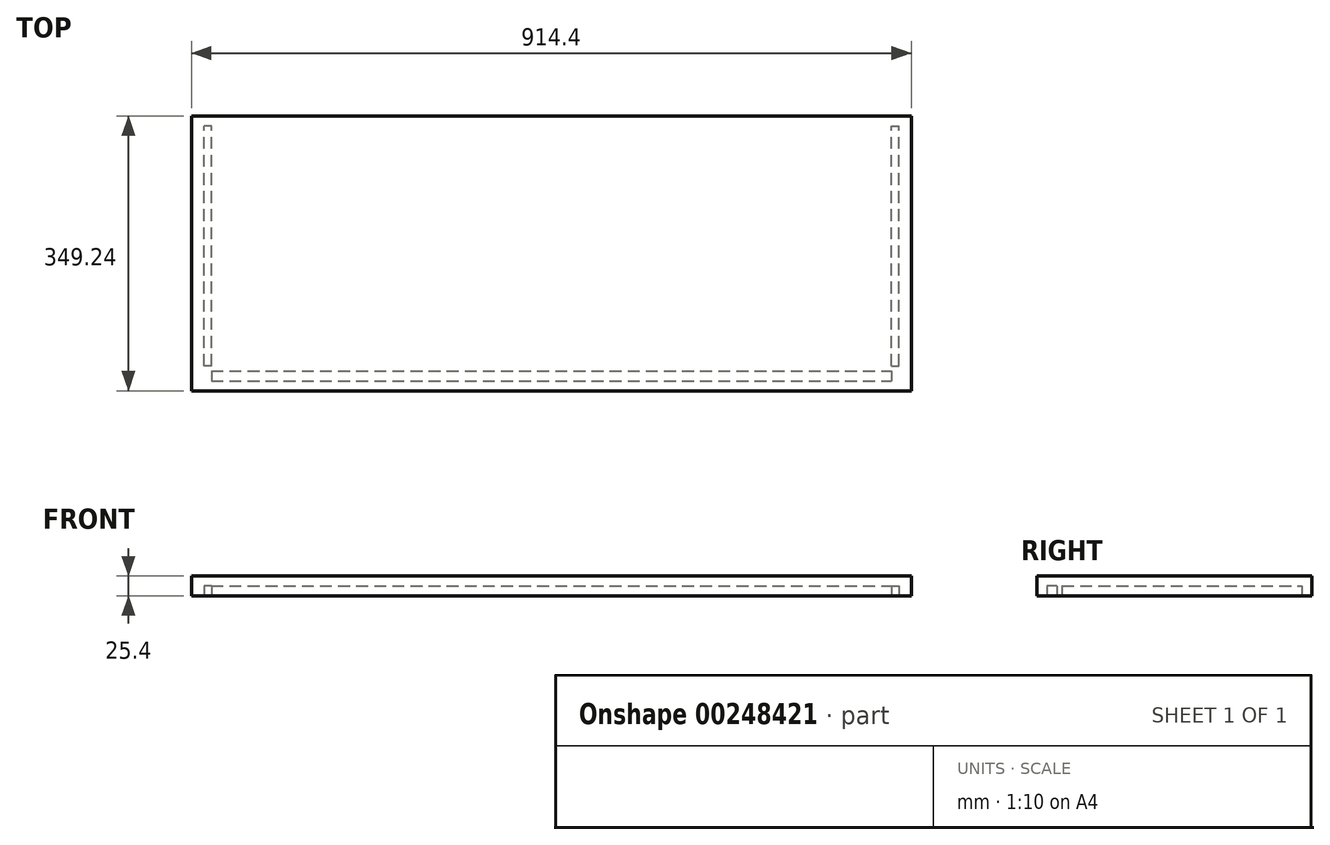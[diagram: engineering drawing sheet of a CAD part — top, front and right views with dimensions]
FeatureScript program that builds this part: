
annotation { "Feature Type Name" : "Feature", "Feature Type Description" : "" }
export const myFeature = defineFeature(function(context is Context, id is Id, definition is map)
    precondition{}
    {
        {
            var Q0;
            Q0=qCreatedBy(makeId("Top.planeOp"),FACE);
            var sketch = newSketch(context, id + "F0", { "sketchPlane" : qUnion([Q0])});
            skLineSegment(sketch, "E0.bottom", {"start": v(-457.2, 174.62) * mm, "end": v(457.2, 174.62) * mm});
            skLineSegment(sketch, "E0.top", {"start": v(-457.2, -174.62) * mm, "end": v(457.2, -174.62) * mm});
            skLineSegment(sketch, "E0.left", {"start": v(-457.2, 174.62) * mm, "end": v(-457.2, -174.62) * mm});
            skLineSegment(sketch, "E0.right", {"start": v(457.2, 174.62) * mm, "end": v(457.2, -174.62) * mm});
            skPoint(sketch, "E0.middle", {"position": v(0, 0) * mm});
            skSolve(sketch);
        }
        {
            var Q0;
            Q0=makeQuery(id+"F0.imprint","IMPRINT",FACE,{"disambiguationData":[TD([[makeQuery(id+"F0.imprint","IMPRINT",EDGE,{"derivedFrom":sQuery(id+"F0.wireOp",EDGE,"E0.bottom")}),-1.0]])]});
            var Q1;
            Q1=makeQuery(id+"F0.imprint","IMPRINT",FACE,{"disambiguationData":[TD([[makeQuery(id+"F0.imprint","IMPRINT",EDGE,{"derivedFrom":sQuery(id+"F0.wireOp",EDGE,"0kOpWPuX-2Et7-S9QX-p4uN-rlqqt7OtT0GP")}),1.0]])]});
            extrude(context, id + "F1", {"entities" : qUnion([Q0, Q1]), "endBound" : BoundingType.SYMMETRIC, "depth" : 25.4 * mm});
        }
        {
            var Q0;
            Q0=makeQuery(id+"F1.opExtrude","CAP_FACE",FACE,{"disambiguationData":[OSD([sQuery(id+"F0.wireOp",EDGE,"E0.bottom"),sQuery(id+"F0.wireOp",EDGE,"E0.top"),sQuery(id+"F0.wireOp",EDGE,"E0.left"),sQuery(id+"F0.wireOp",EDGE,"E0.right")])],"isStart":true});
            var sketch = newSketch(context, id + "F2", { "sketchPlane" : qUnion([Q0])});
            skLineSegment(sketch, "E1", {"start": v(-431.8, 149.23) * mm, "end": v(431.8, 149.23) * mm});
            skLineSegment(sketch, "E2", {"start": v(-431.8, 161.93) * mm, "end": v(431.8, 161.93) * mm});
            skLineSegment(sketch, "E3", {"start": v(-431.8, 149.23) * mm, "end": v(-431.8, 161.93) * mm});
            skLineSegment(sketch, "E4", {"start": v(431.8, 149.23) * mm, "end": v(431.8, 161.93) * mm});
            skSolve(sketch);
        }
        {
            var Q0;
            Q0=makeQuery(id+"F2.imprint","IMPRINT",FACE,{"disambiguationData":[TD([[makeQuery(id+"F2.imprint","IMPRINT",EDGE,{"derivedFrom":sQuery(id+"F2.wireOp",EDGE,"E1")}),1.0]])]});
            extrude(context, id + "F3", {"entities" : qUnion([Q0]), "operationType" : NewBodyOperationType.REMOVE, "oppositeDirection" : true, "depth" : 12.7 * mm});
        }
        {
            var Q0;
            Q0=makeQuery(id+"F1.opExtrude","CAP_FACE",FACE,{"disambiguationData":[OSD([sQuery(id+"F0.wireOp",EDGE,"E0.bottom"),sQuery(id+"F0.wireOp",EDGE,"E0.top"),sQuery(id+"F0.wireOp",EDGE,"E0.left"),sQuery(id+"F0.wireOp",EDGE,"E0.right")])],"isStart":true});
            var sketch = newSketch(context, id + "F4", { "sketchPlane" : qUnion([Q0])});
            skLineSegment(sketch, "E5", {"start": v(-431.8, 142.88) * mm, "end": v(-431.8, -161.93) * mm});
            skLineSegment(sketch, "E6", {"start": v(-441.33, 142.88) * mm, "end": v(-441.33, -161.93) * mm});
            skLineSegment(sketch, "E7", {"start": v(-431.8, 142.88) * mm, "end": v(-441.33, 142.88) * mm});
            skLineSegment(sketch, "E8", {"start": v(-431.8, -161.93) * mm, "end": v(-441.33, -161.93) * mm});
            skLineSegment(sketch, "E9.MirrorCS", {"start": v(431.8, 142.88) * mm, "end": v(431.8, -161.93) * mm});
            skLineSegment(sketch, "E10.MirrorCS", {"start": v(441.33, 142.88) * mm, "end": v(441.33, -161.93) * mm});
            skLineSegment(sketch, "E11.MirrorCS", {"start": v(431.8, 142.88) * mm, "end": v(441.33, 142.88) * mm});
            skLineSegment(sketch, "E12.MirrorCS", {"start": v(431.8, -161.93) * mm, "end": v(441.33, -161.93) * mm});
            skSolve(sketch);
        }
        {
            var Q0;
            Q0=makeQuery(id+"F4.imprint","IMPRINT",FACE,{"disambiguationData":[TD([[makeQuery(id+"F4.imprint","IMPRINT",EDGE,{"derivedFrom":sQuery(id+"F4.wireOp",EDGE,"E5")}),-1.0]])]});
            var Q1;
            Q1=makeQuery(id+"F4.imprint","IMPRINT",FACE,{"disambiguationData":[TD([[makeQuery(id+"F4.imprint","IMPRINT",EDGE,{"derivedFrom":sQuery(id+"F4.wireOp",EDGE,"E9.MirrorCS")}),1.0]])]});
            extrude(context, id + "F5", {"entities" : qUnion([Q0, Q1]), "operationType" : NewBodyOperationType.REMOVE, "oppositeDirection" : true, "depth" : 12.7 * mm});
        }
    });
